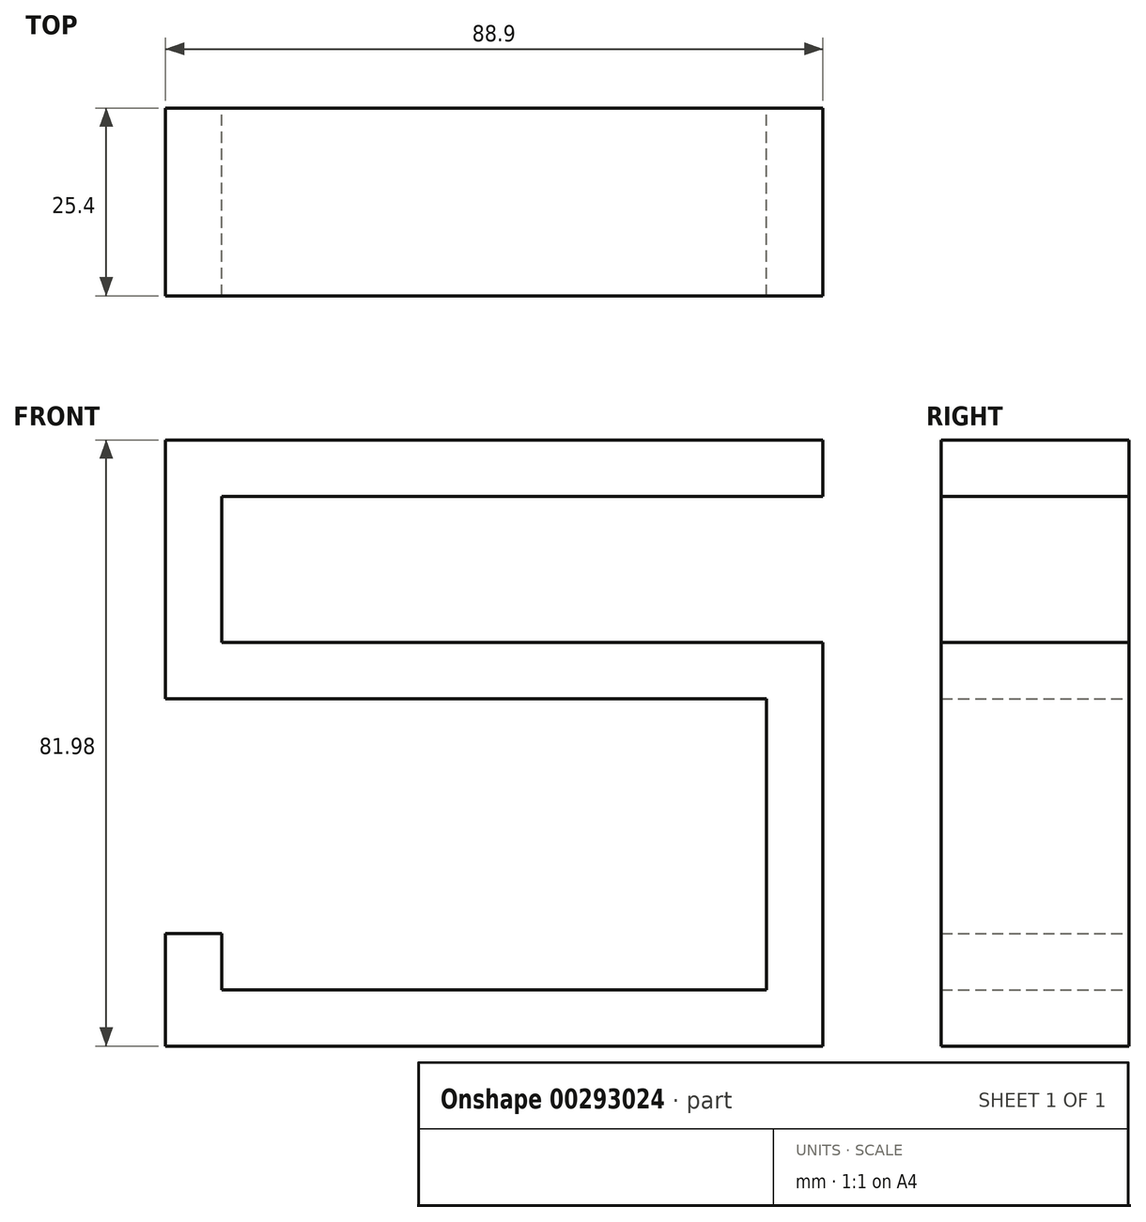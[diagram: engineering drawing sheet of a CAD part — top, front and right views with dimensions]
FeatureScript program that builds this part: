
annotation { "Feature Type Name" : "Feature", "Feature Type Description" : "" }
export const myFeature = defineFeature(function(context is Context, id is Id, definition is map)
    precondition{}
    {
        {
            var Q0;
            Q0=qCreatedBy(makeId("Front.planeOp"),FACE);
            var sketch = newSketch(context, id + "F0", { "sketchPlane" : qUnion([Q0])});
            skLineSegment(sketch, "E0.bottom", {"start": v(59.84, 45.76) * mm, "end": v(-29.06, 45.76) * mm});
            skLineSegment(sketch, "E0.top", {"start": v(59.84, 38.14) * mm, "end": v(-21.44, 38.14) * mm});
            skLineSegment(sketch, "E0.left", {"start": v(59.84, 45.76) * mm, "end": v(59.84, 38.14) * mm});
            skLineSegment(sketch, "E0.right", {"start": v(-29.06, 45.76) * mm, "end": v(-29.06, 38.14) * mm});
            skLineSegment(sketch, "E1.top", {"start": v(-29.06, 10.77) * mm, "end": v(-21.44, 10.77) * mm});
            skLineSegment(sketch, "E1.left", {"start": v(-29.06, 38.14) * mm, "end": v(-29.06, 10.77) * mm});
            skLineSegment(sketch, "E1.right", {"start": v(-21.44, 38.14) * mm, "end": v(-21.44, 18.4) * mm});
            skLineSegment(sketch, "E2.bottom", {"start": v(-21.44, 10.77) * mm, "end": v(52.22, 10.77) * mm});
            skLineSegment(sketch, "E2.top", {"start": v(-21.44, 18.4) * mm, "end": v(59.84, 18.4) * mm});
            skLineSegment(sketch, "E2.right", {"start": v(59.84, 10.77) * mm, "end": v(59.84, 18.4) * mm});
            skLineSegment(sketch, "E3.left", {"start": v(59.84, 10.77) * mm, "end": v(59.84, -28.6) * mm});
            skLineSegment(sketch, "E3.right", {"start": v(52.22, 10.77) * mm, "end": v(52.22, -28.6) * mm});
            skLineSegment(sketch, "E4.bottom", {"start": v(59.84, -36.22) * mm, "end": v(-29.06, -36.22) * mm});
            skLineSegment(sketch, "E4.top", {"start": v(52.22, -28.6) * mm, "end": v(-21.44, -28.6) * mm});
            skLineSegment(sketch, "E4.left", {"start": v(59.84, -36.22) * mm, "end": v(59.84, -28.6) * mm});
            skLineSegment(sketch, "E4.right", {"start": v(-29.06, -36.22) * mm, "end": v(-29.06, -28.6) * mm});
            skLineSegment(sketch, "E5.top", {"start": v(-29.06, -20.98) * mm, "end": v(-21.44, -20.98) * mm});
            skLineSegment(sketch, "E5.left", {"start": v(-29.06, -28.6) * mm, "end": v(-29.06, -20.98) * mm});
            skLineSegment(sketch, "E5.right", {"start": v(-21.44, -28.6) * mm, "end": v(-21.44, -20.98) * mm});
            skLineSegment(sketch, "E6", {"start": v(59.84, 18.4) * mm, "end": v(59.84, 45.76) * mm, "construction": true});
            skLineSegment(sketch, "E7", {"start": v(-29.06, 10.77) * mm, "end": v(-29.06, -20.98) * mm, "construction": true});
            skSolve(sketch);
        }
        {
            var Q0;
            Q0 = qSketchRegion(id + "F0", true);
            extrude(context, id + "F1", {"entities" : qUnion([Q0]), "depth" : 25.4 * mm});
        }
    });
